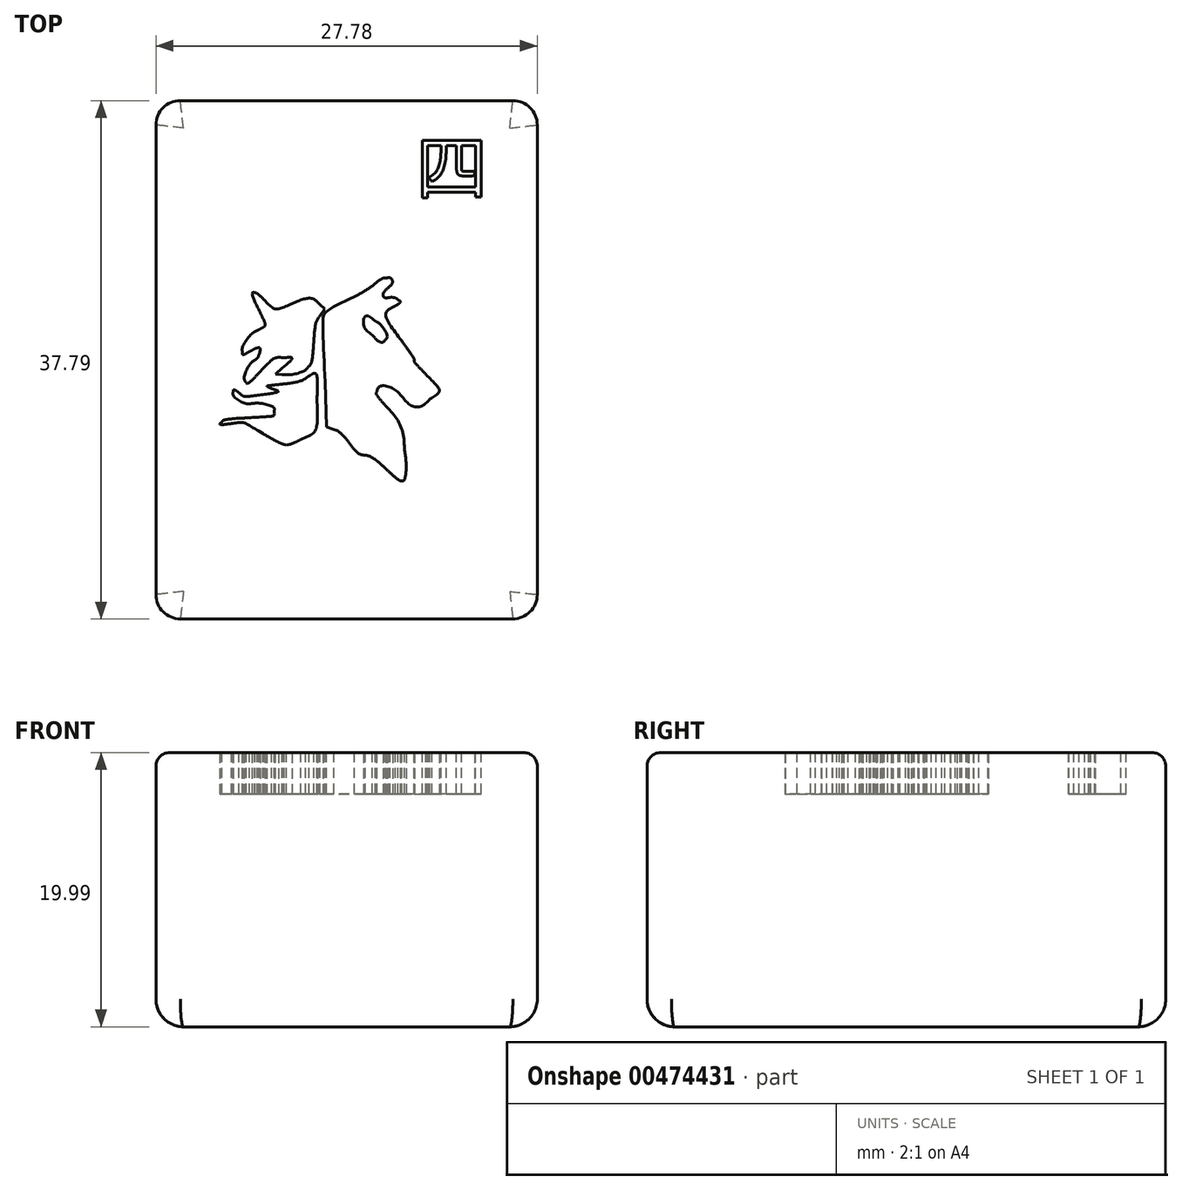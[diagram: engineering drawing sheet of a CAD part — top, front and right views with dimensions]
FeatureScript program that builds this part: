
annotation { "Feature Type Name" : "Feature", "Feature Type Description" : "" }
export const myFeature = defineFeature(function(context is Context, id is Id, definition is map)
    precondition{}
    {
        {
            var Q0;
            Q0=qCreatedBy(makeId("Top.planeOp"),FACE);
            var sketch = newSketch(context, id + "F0", { "sketchPlane" : qUnion([Q0])});
            skLineSegment(sketch, "E0", {"start": v(-13.9, 17.44) * mm, "end": v(-13.9, -16.8) * mm});
            skLineSegment(sketch, "E1", {"start": v(-12.12, -18.58) * mm, "end": v(12.12, -18.58) * mm});
            skLineSegment(sketch, "E2", {"start": v(-12.12, 19.21) * mm, "end": v(12.12, 19.21) * mm});
            skLineSegment(sketch, "E3", {"start": v(13.9, 17.44) * mm, "end": v(13.9, -16.8) * mm});
            skPoint(sketch, "E4.visualSharp", {"position": v(-13.9, 19.21) * mm});
            skArc(sketch, "E4.filletArc", {"start": v(-12.12, 19.21) * mm, "mid": v(-13.37, 18.7) * mm, "end": v(-13.9, 17.44) * mm});
            skPoint(sketch, "E5.visualSharp", {"position": v(13.9, 19.21) * mm});
            skArc(sketch, "E5.filletArc", {"start": v(13.9, 17.44) * mm, "mid": v(13.37, 18.7) * mm, "end": v(12.12, 19.21) * mm});
            skPoint(sketch, "E6.visualSharp", {"position": v(13.9, -18.58) * mm});
            skArc(sketch, "E6.filletArc", {"start": v(12.12, -18.58) * mm, "mid": v(13.37, -18.06) * mm, "end": v(13.9, -16.8) * mm});
            skPoint(sketch, "E7.visualSharp", {"position": v(-13.9, -18.58) * mm});
            skArc(sketch, "E7.filletArc", {"start": v(-13.9, -16.8) * mm, "mid": v(-13.37, -18.06) * mm, "end": v(-12.12, -18.58) * mm});
            skLineSegment(sketch, "E8", {"start": v(0, 0) * mm, "end": v(13.9, 0) * mm});
            skLineSegment(sketch, "E9", {"start": v(13.9, 0) * mm, "end": v(-13.9, 0) * mm});
            skLineSegment(sketch, "E10", {"start": v(0, 0) * mm, "end": v(0, 19.21) * mm});
            skLineSegment(sketch, "E11", {"start": v(0, 19.21) * mm, "end": v(0, -18.58) * mm});
            skSolve(sketch);
        }
        {
            var Q0;
            Q0 = qSketchRegion(id + "F0", true);
            extrude(context, id + "F1", {"entities" : qUnion([Q0]), "depth" : 19.99 * mm, "offsetDistance" : 25.4 * mm});
        }
        {
            var Q0;
            Q0=makeQuery(id+"F1.opExtrude","CAP_EDGE",EDGE,{"disambiguationData":[OSD([sQuery(id+"F0.wireOp",EDGE,"E1")])],"isStart":false});
            var Q1;
            Q1=makeQuery(id+"F1.opExtrude","CAP_EDGE",EDGE,{"disambiguationData":[OSD([sQuery(id+"F0.wireOp",EDGE,"E3")])],"isStart":false});
            var Q2;
            Q2=makeQuery(id+"F1.opExtrude","CAP_EDGE",EDGE,{"disambiguationData":[OSD([sQuery(id+"F0.wireOp",EDGE,"E2")])],"isStart":false});
            var Q3;
            Q3=makeQuery(id+"F1.opExtrude","CAP_EDGE",EDGE,{"disambiguationData":[OSD([sQuery(id+"F0.wireOp",EDGE,"E0")])],"isStart":false});
            var Q4;
            Q4=makeQuery(id+"F1.opExtrude","CAP_FACE",FACE,{"disambiguationData":[OSD([sQuery(id+"F0.wireOp",EDGE,"E0"),sQuery(id+"F0.wireOp",EDGE,"E1"),sQuery(id+"F0.wireOp",EDGE,"E2"),sQuery(id+"F0.wireOp",EDGE,"E3"),sQuery(id+"F0.wireOp",EDGE,"E4.filletArc"),sQuery(id+"F0.wireOp",EDGE,"E5.filletArc"),sQuery(id+"F0.wireOp",EDGE,"E6.filletArc"),sQuery(id+"F0.wireOp",EDGE,"E7.filletArc")])],"isStart":false});
            fillet(context, id + "F2", {"entities" : qUnion([Q0, Q1, Q2, Q3, Q4]), "radius" : 1 * mm, "tangentPropagation" : true, "allowEdgeOverflow" : false});
        }
        {
            var Q0;
            Q0=makeQuery(id+"F1.opExtrude","CAP_EDGE",EDGE,{"disambiguationData":[OSD([sQuery(id+"F0.wireOp",EDGE,"E3")])],"isStart":true});
            var Q1;
            Q1=makeQuery(id+"F1.opExtrude","CAP_EDGE",EDGE,{"disambiguationData":[OSD([sQuery(id+"F0.wireOp",EDGE,"E2")])],"isStart":true});
            var Q2;
            Q2=makeQuery(id+"F1.opExtrude","CAP_FACE",FACE,{"disambiguationData":[OSD([sQuery(id+"F0.wireOp",EDGE,"E0"),sQuery(id+"F0.wireOp",EDGE,"E1"),sQuery(id+"F0.wireOp",EDGE,"E2"),sQuery(id+"F0.wireOp",EDGE,"E3"),sQuery(id+"F0.wireOp",EDGE,"E4.filletArc"),sQuery(id+"F0.wireOp",EDGE,"E5.filletArc"),sQuery(id+"F0.wireOp",EDGE,"E6.filletArc"),sQuery(id+"F0.wireOp",EDGE,"E7.filletArc")])],"isStart":true});
            var Q3;
            Q3=makeQuery(id+"F1.opExtrude","CAP_EDGE",EDGE,{"disambiguationData":[OSD([sQuery(id+"F0.wireOp",EDGE,"E1")])],"isStart":true});
            fillet(context, id + "F3", {"entities" : qUnion([Q0, Q1, Q2, Q3]), "radius" : 2 * mm, "tangentPropagation" : true, "allowEdgeOverflow" : false});
        }
        {
            var Q0;
            Q0=makeQuery(id+"F1.opExtrude","CAP_FACE",FACE,{"disambiguationData":[OSD([sQuery(id+"F0.wireOp",EDGE,"E0"),sQuery(id+"F0.wireOp",EDGE,"E1"),sQuery(id+"F0.wireOp",EDGE,"E2"),sQuery(id+"F0.wireOp",EDGE,"E3"),sQuery(id+"F0.wireOp",EDGE,"E4.filletArc"),sQuery(id+"F0.wireOp",EDGE,"E5.filletArc"),sQuery(id+"F0.wireOp",EDGE,"E6.filletArc"),sQuery(id+"F0.wireOp",EDGE,"E7.filletArc")])],"isStart":false});
            var sketch = newSketch(context, id + "F4", { "sketchPlane" : qUnion([Q0])});
            skText(sketch, "E12", { "text": "四", "fontName": "NotoSansCJKsc-Regular.otf"});
            const initialGuessF4  = {"E12": [0.00503, 0.01236, 1, 0, 0.0038]};
            skSetInitialGuess(sketch, initialGuessF4);
            skSolve(sketch);
        }
        {
            var Q0;
            Q0 = qSketchRegion(id + "F4", true);
            extrude(context, id + "F5", {"entities" : qUnion([Q0]), "operationType" : NewBodyOperationType.REMOVE, "oppositeDirection" : true, "depth" : 3 * mm, "offsetDistance" : 25.4 * mm});
        }
        {
            var Q0;
            Q0=makeQuery(id+"F4.imprint","IMPRINT",FACE,{"disambiguationData":[TD([[makeQuery(id+"F4.imprint","IMPRINT",EDGE,{"derivedFrom":sQuery(id+"F4.wireOp",EDGE,"E12.sketch_text.stroke-18")}),-1.0]])]});
            var sketch = newSketch(context, id + "F6", { "sketchPlane" : qUnion([Q0])});
            skFitSpline(sketch, "E13", {"points": [v(2.84, -7.62) * mm, v(2.3, -7.13) * mm, v(1.66, -6.7) * mm, v(1.35, -6.65) * mm]});
            skFitSpline(sketch, "E14", {"points": [v(1.35, -6.65) * mm, v(0.98, -6.57) * mm, v(0.61, -6.3) * mm, v(0.2, -5.75) * mm]});
            skFitSpline(sketch, "E15", {"points": [v(0.2, -5.75) * mm, v(-0.15, -5.32) * mm, v(-0.65, -4.88) * mm, v(-0.94, -4.77) * mm]});
            skFitSpline(sketch, "E16", {"points": [v(-1.57, -1.3) * mm, v(-1.72, 3.15) * mm, v(-1.51, 3.8) * mm, v(0.56, 4.9) * mm]});
            skFitSpline(sketch, "E17", {"points": [v(0.56, 4.9) * mm, v(1.1, 5.2) * mm, v(1.78, 5.63) * mm, v(2.06, 5.86) * mm]});
            skFitSpline(sketch, "E18", {"points": [v(2.06, 5.86) * mm, v(2.34, 6.08) * mm, v(2.69, 6.27) * mm, v(2.83, 6.27) * mm]});
            skFitSpline(sketch, "E19", {"points": [v(2.83, 6.27) * mm, v(3.23, 6.27) * mm, v(3.34, 5.93) * mm, v(3.05, 5.59) * mm]});
            skFitSpline(sketch, "E20", {"points": [v(3.05, 5.59) * mm, v(2.68, 5.15) * mm, v(2.72, 4.87) * mm, v(3.16, 4.86) * mm]});
            skFitSpline(sketch, "E21", {"points": [v(3.16, 4.86) * mm, v(3.37, 4.86) * mm, v(3.63, 4.79) * mm, v(3.76, 4.7) * mm]});
            skFitSpline(sketch, "E22", {"points": [v(3.76, 4.7) * mm, v(3.93, 4.56) * mm, v(3.9, 4.47) * mm, v(3.55, 4.24) * mm]});
            skFitSpline(sketch, "E23", {"points": [v(3.55, 4.24) * mm, v(2.88, 3.76) * mm, v(2.99, 3.17) * mm, v(4.02, 1.7) * mm]});
            skFitSpline(sketch, "E24", {"points": [v(4.02, 1.7) * mm, v(4.52, 0.98) * mm, v(4.93, 0.34) * mm, v(4.93, 0.27) * mm]});
            skFitSpline(sketch, "E25", {"points": [v(4.93, 0.27) * mm, v(4.93, 0.2) * mm, v(5.3, -0.26) * mm, v(5.77, -0.75) * mm]});
            skFitSpline(sketch, "E26", {"points": [v(5.77, -0.75) * mm, v(6.68, -1.73) * mm, v(6.73, -2.04) * mm, v(6.07, -2.56) * mm]});
            skFitSpline(sketch, "E27", {"points": [v(6.07, -2.56) * mm, v(5.42, -3.08) * mm, v(4.72, -3.02) * mm, v(4.03, -2.37) * mm]});
            skFitSpline(sketch, "E28", {"points": [v(4.03, -2.37) * mm, v(3.42, -1.8) * mm, v(2.44, -1.6) * mm, v(2.2, -2) * mm]});
            skFitSpline(sketch, "E29", {"points": [v(2.2, -2) * mm, v(2.15, -2.12) * mm, v(2.41, -2.54) * mm, v(2.8, -2.98) * mm]});
            skFitSpline(sketch, "E30", {"points": [v(2.8, -2.98) * mm, v(3.63, -3.95) * mm, v(4.1, -5.05) * mm, v(4.22, -6.3) * mm]});
            skFitSpline(sketch, "E31", {"points": [v(4.22, -6.3) * mm, v(4.34, -7.32) * mm, v(4.17, -8.5) * mm, v(3.95, -8.5) * mm]});
            skFitSpline(sketch, "E32", {"points": [v(3.95, -8.5) * mm, v(3.87, -8.5) * mm, v(3.38, -8.1) * mm, v(2.86, -7.63) * mm]});
            skLineSegment(sketch, "E33", {"start": v(-0.94, -4.77) * mm, "end": v(-1.45, -4.57) * mm});
            skLineSegment(sketch, "E34", {"start": v(-1.45, -4.57) * mm, "end": v(-1.57, -1.3) * mm});
            skFitSpline(sketch, "E35", {"points": [v(2.83, 1.81) * mm, v(2.97, 1.99) * mm, v(2.43, 2.93) * mm, v(2.08, 3.13) * mm]});
            skFitSpline(sketch, "E36", {"points": [v(2.08, 3.13) * mm, v(1.4, 3.52) * mm, v(1.25, 2.79) * mm, v(1.87, 2.13) * mm]});
            skFitSpline(sketch, "E37", {"points": [v(1.87, 2.13) * mm, v(2.27, 1.7) * mm, v(2.63, 1.6) * mm, v(2.83, 1.81) * mm]});
            skLineSegment(sketch, "E38", {"start": v(2.86, -7.63) * mm, "end": v(2.84, -7.62) * mm});
            skFitSpline(sketch, "E39", {"points": [v(-6.1, -5.04) * mm, v(-7.4, -4.3) * mm, v(-7.58, -4.25) * mm, v(-8.4, -4.33) * mm]});
            skFitSpline(sketch, "E40", {"points": [v(-8.4, -4.33) * mm, v(-9.08, -4.41) * mm, v(-9.24, -4.37) * mm, v(-9.1, -4.22) * mm]});
            skFitSpline(sketch, "E41", {"points": [v(-9.1, -4.22) * mm, v(-8.98, -4.1) * mm, v(-8.18, -3.97) * mm, v(-7.3, -3.92) * mm]});
            skFitSpline(sketch, "E42", {"points": [v(-7.3, -3.92) * mm, v(-5.75, -3.83) * mm, v(-5.28, -3.71) * mm, v(-5.28, -3.4) * mm]});
            skFitSpline(sketch, "E43", {"points": [v(-5.28, -3.4) * mm, v(-5.28, -3.19) * mm, v(-6.23, -2.87) * mm, v(-6.85, -2.87) * mm]});
            skFitSpline(sketch, "E44", {"points": [v(-6.85, -2.87) * mm, v(-7.37, -2.87) * mm, v(-8.25, -2.3) * mm, v(-8.25, -1.97) * mm]});
            skFitSpline(sketch, "E45", {"points": [v(-8.25, -1.97) * mm, v(-8.25, -1.88) * mm, v(-8.06, -1.93) * mm, v(-7.84, -2.1) * mm]});
            skFitSpline(sketch, "E46", {"points": [v(-7.84, -2.1) * mm, v(-7.52, -2.33) * mm, v(-7.22, -2.36) * mm, v(-6.5, -2.28) * mm]});
            skFitSpline(sketch, "E47", {"points": [v(-6.5, -2.28) * mm, v(-5.2, -2.08) * mm, v(-4.97, -2) * mm, v(-5.46, -1.77) * mm]});
            skFitSpline(sketch, "E48", {"points": [v(-5.46, -1.77) * mm, v(-5.8, -1.62) * mm, v(-5.68, -1.58) * mm, v(-4.67, -1.45) * mm]});
            skFitSpline(sketch, "E49", {"points": [v(-4.67, -1.45) * mm, v(-4.01, -1.38) * mm, v(-3.26, -1.2) * mm, v(-3, -1.05) * mm]});
            skFitSpline(sketch, "E50", {"points": [v(-3, -1.05) * mm, v(-2.31, -0.67) * mm, v(-2.15, -0.96) * mm, v(-2.15, -2.57) * mm]});
            skFitSpline(sketch, "E51", {"points": [v(-2.15, -2.57) * mm, v(-2.15, -4.39) * mm, v(-2.41, -5.01) * mm, v(-3.34, -5.5) * mm]});
            skFitSpline(sketch, "E52", {"points": [v(-3.34, -5.5) * mm, v(-3.74, -5.7) * mm, v(-4.21, -5.87) * mm, v(-4.39, -5.86) * mm]});
            skFitSpline(sketch, "E53", {"points": [v(-4.39, -5.86) * mm, v(-4.56, -5.86) * mm, v(-5.34, -5.5) * mm, v(-6.1, -5.06) * mm]});
            skFitSpline(sketch, "E54", {"points": [v(-7.33, -1.3) * mm, v(-7.46, -1.07) * mm, v(-7.07, -0.04) * mm, v(-6.71, 0.27) * mm]});
            skFitSpline(sketch, "E55", {"points": [v(-6.71, 0.27) * mm, v(-6.46, 0.5) * mm, v(-6.32, 1.17) * mm, v(-6.52, 1.17) * mm]});
            skFitSpline(sketch, "E56", {"points": [v(-6.52, 1.17) * mm, v(-6.58, 1.17) * mm, v(-6.83, 1.04) * mm, v(-7.1, 0.9) * mm]});
            skFitSpline(sketch, "E57", {"points": [v(-7.1, 0.9) * mm, v(-7.43, 0.72) * mm, v(-7.58, 0.7) * mm, v(-7.58, 0.83) * mm]});
            skFitSpline(sketch, "E58", {"points": [v(-7.58, 0.83) * mm, v(-7.58, 1.24) * mm, v(-6.88, 2.23) * mm, v(-6.41, 2.5) * mm]});
            skFitSpline(sketch, "E59", {"points": [v(-6.41, 2.5) * mm, v(-6.15, 2.64) * mm, v(-5.94, 2.81) * mm, v(-5.94, 2.88) * mm]});
            skFitSpline(sketch, "E60", {"points": [v(-5.94, 2.88) * mm, v(-5.94, 2.96) * mm, v(-6.13, 3.4) * mm, v(-6.35, 3.87) * mm]});
            skFitSpline(sketch, "E61", {"points": [v(-6.35, 3.87) * mm, v(-6.75, 4.72) * mm, v(-6.86, 5.2) * mm, v(-6.66, 5.2) * mm]});
            skFitSpline(sketch, "E62", {"points": [v(-6.66, 5.2) * mm, v(-6.6, 5.2) * mm, v(-6.3, 4.97) * mm, v(-6, 4.68) * mm]});
            skFitSpline(sketch, "E63", {"points": [v(-6, 4.68) * mm, v(-5.36, 4.08) * mm, v(-4.97, 4.03) * mm, v(-3.96, 4.41) * mm]});
            skFitSpline(sketch, "E64", {"points": [v(-3.96, 4.41) * mm, v(-3.03, 4.77) * mm, v(-2.43, 4.75) * mm, v(-1.97, 4.36) * mm]});
            skLineSegment(sketch, "E65", {"start": v(-6.1, -5.06) * mm, "end": v(-6.1, -5.04) * mm});
            skFitSpline(sketch, "E66", {"points": [v(-1.94, 3.52) * mm, v(-2.18, 3.16) * mm, v(-2.3, 2.59) * mm, v(-2.4, 1.56) * mm]});
            skFitSpline(sketch, "E67", {"points": [v(-2.4, 1.56) * mm, v(-2.47, 0.68) * mm, v(-2.6, 0) * mm, v(-2.75, -0.15) * mm]});
            skFitSpline(sketch, "E68", {"points": [v(-2.75, -0.15) * mm, v(-3.04, -0.46) * mm, v(-4.03, -0.77) * mm, v(-4.7, -0.76) * mm]});
            skLineSegment(sketch, "E69", {"start": v(-1.97, 4.36) * mm, "end": v(-1.6, 4.03) * mm});
            skLineSegment(sketch, "E70", {"start": v(-1.6, 4.03) * mm, "end": v(-1.94, 3.52) * mm});
            skFitSpline(sketch, "E71", {"points": [v(-4.66, -0.26) * mm, v(-4.01, 0.33) * mm, v(-4, 0.46) * mm, v(-4.55, 0.46) * mm]});
            skFitSpline(sketch, "E72", {"points": [v(-4.55, 0.46) * mm, v(-5.13, 0.46) * mm, v(-5.57, 0.2) * mm, v(-6.45, -0.71) * mm]});
            skFitSpline(sketch, "E73", {"points": [v(-6.45, -0.71) * mm, v(-6.9, -1.18) * mm, v(-7.26, -1.42) * mm, v(-7.32, -1.32) * mm]});
            skLineSegment(sketch, "E74", {"start": v(-4.7, -0.76) * mm, "end": v(-5.2, -0.75) * mm});
            skLineSegment(sketch, "E75", {"start": v(-5.2, -0.75) * mm, "end": v(-4.66, -0.26) * mm});
            skFitSpline(sketch, "E76", {"points": [v(4, 3.04) * mm, v(3.93, 3.2) * mm, v(3.95, 3.37) * mm, v(4.05, 3.43) * mm]});
            skFitSpline(sketch, "E77", {"points": [v(4.05, 3.43) * mm, v(4.84, 4) * mm, v(9.06, 6.8) * mm, v(9.13, 6.8) * mm]});
            skFitSpline(sketch, "E78", {"points": [v(9.13, 6.8) * mm, v(9.27, 6.8) * mm, v(7.98, 5.62) * mm, v(6.15, 4.06) * mm]});
            skFitSpline(sketch, "E79", {"points": [v(6.15, 4.06) * mm, v(4.58, 2.73) * mm, v(4.17, 2.54) * mm, v(4, 3.04) * mm]});
            skLineSegment(sketch, "E80", {"start": v(-7.32, -1.32) * mm, "end": v(-7.33, -1.3) * mm});
            skFitSpline(sketch, "E81", {"points": [v(-1.95, 5.09) * mm, v(-2.64, 5.45) * mm, v(-2.68, 5.46) * mm, v(-3.93, 5.18) * mm]});
            skFitSpline(sketch, "E82", {"points": [v(-5.74, 5.44) * mm, v(-6.32, 6.04) * mm, v(-6.54, 6.76) * mm, v(-5.98, 6.21) * mm]});
            skFitSpline(sketch, "E83", {"points": [v(-5.98, 6.21) * mm, v(-5.3, 5.56) * mm, v(-3.4, 6.17) * mm, v(-3.5, 7.02) * mm]});
            skFitSpline(sketch, "E84", {"points": [v(-3.5, 7.02) * mm, v(-3.55, 7.33) * mm, v(-3.7, 7.43) * mm, v(-4.22, 7.51) * mm]});
            skLineSegment(sketch, "E85", {"start": v(-3.93, 5.18) * mm, "end": v(-5.2, 4.9) * mm});
            skLineSegment(sketch, "E86", {"start": v(-5.2, 4.9) * mm, "end": v(-5.74, 5.44) * mm});
            skFitSpline(sketch, "E87", {"points": [v(-4.42, 7.85) * mm, v(-4.02, 8.06) * mm, v(-3.85, 8.05) * mm, v(-3.15, 7.77) * mm]});
            skFitSpline(sketch, "E88", {"points": [v(-3.15, 7.77) * mm, v(-2.16, 7.4) * mm, v(0.05, 7.18) * mm, v(0.2, 7.46) * mm]});
            skFitSpline(sketch, "E89", {"points": [v(0.2, 7.46) * mm, v(0.27, 7.57) * mm, v(0.23, 7.8) * mm, v(0.11, 8) * mm]});
            skFitSpline(sketch, "E90", {"points": [v(0.11, 8) * mm, v(0, 8.2) * mm, v(-0.04, 8.4) * mm, v(0, 8.46) * mm]});
            skFitSpline(sketch, "E91", {"points": [v(0, 8.46) * mm, v(0.17, 8.65) * mm, v(1.29, 8) * mm, v(1.56, 7.55) * mm]});
            skFitSpline(sketch, "E92", {"points": [v(1.56, 7.55) * mm, v(1.8, 7.18) * mm, v(1.8, 7.1) * mm, v(1.56, 6.73) * mm]});
            skFitSpline(sketch, "E93", {"points": [v(1.56, 6.73) * mm, v(1.43, 6.5) * mm, v(0.95, 6.09) * mm, v(0.51, 5.82) * mm]});
            skFitSpline(sketch, "E94", {"points": [v(0.51, 5.82) * mm, v(0.08, 5.55) * mm, v(-0.46, 5.18) * mm, v(-0.67, 5) * mm]});
            skFitSpline(sketch, "E95", {"points": [v(-0.67, 5) * mm, v(-1.14, 4.62) * mm, v(-1.1, 4.61) * mm, v(-1.97, 5.08) * mm]});
            skLineSegment(sketch, "E96", {"start": v(-4.22, 7.51) * mm, "end": v(-4.88, 7.6) * mm});
            skLineSegment(sketch, "E97", {"start": v(-4.88, 7.6) * mm, "end": v(-4.42, 7.85) * mm});
            skLineSegment(sketch, "E98", {"start": v(-1.97, 5.08) * mm, "end": v(-1.95, 5.09) * mm});
            skLineSegment(sketch, "E99", {"start": v(3.99, 3.04) * mm, "end": v(4, 3.03) * mm});
            skSolve(sketch);
        }
        {
            var Q0;
            Q0=makeQuery(id+"F6.imprint","IMPRINT",FACE,{"disambiguationData":[TD([[makeQuery(id+"F6.imprint","IMPRINT",EDGE,{"derivedFrom":sQuery(id+"F6.wireOp",EDGE,"E13")}),-1.0]])]});
            var Q1;
            Q1=makeQuery(id+"F6.imprint","IMPRINT",FACE,{"disambiguationData":[TD([[makeQuery(id+"F6.imprint","IMPRINT",EDGE,{"derivedFrom":sQuery(id+"F6.wireOp",EDGE,"E76")}),-1.0]])]});
            var Q2;
            Q2=makeQuery(id+"F6.imprint","IMPRINT",FACE,{"disambiguationData":[TD([[makeQuery(id+"F6.imprint","IMPRINT",EDGE,{"derivedFrom":sQuery(id+"F6.wireOp",EDGE,"E81")}),-1.0]])]});
            var Q3;
            Q3=makeQuery(id+"F6.imprint","IMPRINT",FACE,{"disambiguationData":[TD([[makeQuery(id+"F6.imprint","IMPRINT",EDGE,{"derivedFrom":sQuery(id+"F6.wireOp",EDGE,"E54")}),-1.0]])]});
            var Q4;
            Q4=makeQuery(id+"F6.imprint","IMPRINT",FACE,{"disambiguationData":[TD([[makeQuery(id+"F6.imprint","IMPRINT",EDGE,{"derivedFrom":sQuery(id+"F6.wireOp",EDGE,"E39")}),-1.0]])]});
            extrude(context, id + "F7", {"entities" : qUnion([Q0, Q1, Q2, Q3, Q4]), "operationType" : NewBodyOperationType.REMOVE, "oppositeDirection" : true, "depth" : 3 * mm, "offsetDistance" : 25.4 * mm});
        }
    });
